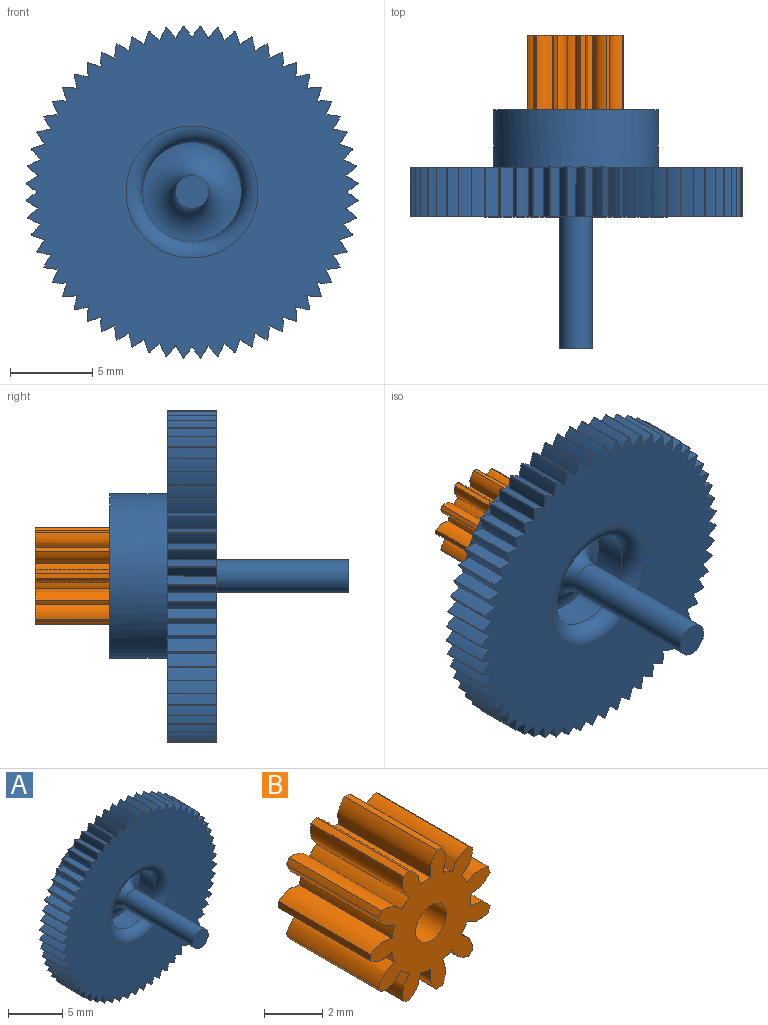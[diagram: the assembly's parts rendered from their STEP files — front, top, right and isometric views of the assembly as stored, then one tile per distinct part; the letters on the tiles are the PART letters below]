
ASSEMBLY  parts=2 mates=1
PART A: 189 faces, bbox 20.1x14.5x20.1 mm
  f0: cylinder r=10.08mm len=3mm, axis (0,1,0), area 0.1mm2, adj f59,f61,f178,f181
  f1: cylinder r=10.08mm len=3mm, axis (0,1,0), area 0.1mm2, adj f59,f61,f176,f179
  f2: cylinder r=10.08mm len=3mm, axis (0,1,0), area 0.1mm2, adj f59,f61,f174,f177
  f3: cylinder r=10.08mm len=3mm, axis (0,1,0), area 0.1mm2, adj f59,f61,f172,f175
  f4: cylinder r=10.08mm len=3mm, axis (0,1,0), area 0.1mm2, adj f59,f61,f170,f173
  f5: cylinder r=10.08mm len=3mm, axis (0,1,0), area 0.1mm2, adj f59,f61,f168,f171
  f6: cylinder r=10.08mm len=3mm, axis (0,1,0), area 0.1mm2, adj f59,f61,f166,f169
  f7: cylinder r=10.08mm len=3mm, axis (0,1,0), area 0.1mm2, adj f59,f61,f160,f167
  f8: cylinder r=10.08mm len=3mm, axis (0,1,0), area 0.1mm2, adj f59,f61,f156,f165
  f9: cylinder r=10.08mm len=3mm, axis (0,1,0), area 0.1mm2, adj f59,f61,f163,f164
  f10: cylinder r=10.08mm len=3mm, axis (0,1,0), area 0.1mm2, adj f59,f61,f158,f161
  f11: cylinder r=10.08mm len=3mm, axis (0,1,0), area 0.1mm2, adj f59,f61,f159,f162
  f12: cylinder r=10.08mm len=3mm, axis (0,1,0), area 0.1mm2, adj f59,f61,f154,f157
  f13: cylinder r=10.08mm len=3mm, axis (0,1,0), area 0.1mm2, adj f59,f61,f152,f155
  f14: cylinder r=10.08mm len=3mm, axis (0,1,0), area 0.1mm2, adj f59,f61,f150,f153
  f15: cylinder r=10.08mm len=3mm, axis (0,1,0), area 0.1mm2, adj f59,f61,f62,f151
  f16: cylinder r=10.08mm len=3mm, axis (0,1,0), area 0.1mm2, adj f59,f61,f149,f180
  f17: cylinder r=10.08mm len=3mm, axis (0,1,0), area 0.1mm2, adj f59,f61,f147,f148
  f18: cylinder r=10.08mm len=3mm, axis (0,1,0), area 0.1mm2, adj f59,f61,f145,f146
  f19: cylinder r=10.08mm len=3mm, axis (0,1,0), area 0.1mm2, adj f59,f61,f143,f144
  f20: cylinder r=10.08mm len=3mm, axis (0,1,0), area 0.1mm2, adj f59,f61,f134,f141
  f21: cylinder r=10.08mm len=3mm, axis (0,1,0), area 0.1mm2, adj f59,f61,f139,f140
  f22: cylinder r=10.08mm len=3mm, axis (0,1,0), area 0.1mm2, adj f59,f61,f137,f142
  f23: cylinder r=10.08mm len=3mm, axis (0,1,0), area 0.1mm2, adj f59,f61,f135,f136
  f24: cylinder r=10.08mm len=3mm, axis (0,1,0), area 0.1mm2, adj f59,f61,f133,f138
  f25: cylinder r=10.08mm len=3mm, axis (0,1,0), area 0.1mm2, adj f59,f61,f131,f132
  f26: cylinder r=10.08mm len=3mm, axis (0,1,0), area 0.1mm2, adj f59,f61,f129,f130
  f27: cylinder r=10.08mm len=3mm, axis (0,1,0), area 0.1mm2, adj f59,f61,f127,f128
  f28: cylinder r=10.08mm len=3mm, axis (0,1,0), area 0.1mm2, adj f59,f61,f125,f126
  f29: cylinder r=10.08mm len=3mm, axis (0,1,0), area 0.1mm2, adj f59,f61,f123,f124
  f30: cylinder r=10.08mm len=3mm, axis (0,1,0), area 0.1mm2, adj f59,f61,f121,f122
  f31: cylinder r=10.08mm len=3mm, axis (0,1,0), area 0.1mm2, adj f59,f61,f119,f120
  f32: cylinder r=10.08mm len=3mm, axis (0,1,0), area 0.1mm2, adj f59,f61,f114,f117
  f33: cylinder r=10.08mm len=3mm, axis (0,1,0), area 0.1mm2, adj f59,f61,f108,f115
  f34: cylinder r=10.08mm len=3mm, axis (0,1,0), area 0.1mm2, adj f59,f61,f113,f116
  f35: cylinder r=10.08mm len=3mm, axis (0,1,0), area 0.1mm2, adj f59,f61,f111,f112
  f36: cylinder r=10.08mm len=3mm, axis (0,1,0), area 0.1mm2, adj f59,f61,f106,f109
  f37: cylinder r=10.08mm len=3mm, axis (0,1,0), area 0.1mm2, adj f59,f61,f104,f107
  f38: cylinder r=10.08mm len=3mm, axis (0,1,0), area 0.1mm2, adj f59,f61,f102,f105
  f39: cylinder r=10.08mm len=3mm, axis (0,1,0), area 0.1mm2, adj f59,f61,f103,f118
  f40: cylinder r=10.08mm len=3mm, axis (0,1,0), area 0.1mm2, adj f59,f61,f101,f110
  f41: cylinder r=10.08mm len=3mm, axis (0,1,0), area 0.1mm2, adj f59,f61,f99,f100
  f42: cylinder r=10.08mm len=3mm, axis (0,1,0), area 0.1mm2, adj f59,f61,f97,f98
  f43: cylinder r=10.08mm len=3mm, axis (0,1,0), area 0.1mm2, adj f59,f61,f95,f96
  f44: cylinder r=10.08mm len=3mm, axis (0,1,0), area 0.1mm2, adj f59,f61,f93,f94
  f45: cylinder r=10.08mm len=3mm, axis (0,1,0), area 0.1mm2, adj f59,f61,f91,f92
  f46: cylinder r=10.08mm len=3mm, axis (0,1,0), area 0.1mm2, adj f59,f61,f89,f90
  f47: cylinder r=10.08mm len=3mm, axis (0,1,0), area 0.1mm2, adj f59,f61,f87,f88
  f48: cylinder r=10.08mm len=3mm, axis (0,1,0), area 0.1mm2, adj f59,f61,f82,f85
  f49: cylinder r=10.08mm len=3mm, axis (0,1,0), area 0.1mm2, adj f59,f61,f78,f83
  f50: cylinder r=10.08mm len=3mm, axis (0,1,0), area 0.1mm2, adj f59,f61,f74,f81
  f51: cylinder r=10.08mm len=3mm, axis (0,1,0), area 0.1mm2, adj f59,f61,f79,f80
  f52: cylinder r=10.08mm len=3mm, axis (0,1,0), area 0.1mm2, adj f59,f61,f72,f77
  f53: cylinder r=10.08mm len=3mm, axis (0,1,0), area 0.1mm2, adj f59,f61,f75,f76
  f54: cylinder r=10.08mm len=3mm, axis (0,1,0), area 0.1mm2, adj f59,f61,f70,f73
  f55: cylinder r=10.08mm len=3mm, axis (0,1,0), area 0.1mm2, adj f59,f61,f71,f86
  f56: cylinder r=10.08mm len=3mm, axis (0,1,0), area 0.1mm2, adj f59,f61,f69,f84
  f57: cylinder r=10.08mm len=3mm, axis (0,1,0), area 0.1mm2, adj f59,f61,f67,f68
  f58: cylinder r=10.08mm len=3mm, axis (0,1,0), area 0.1mm2, adj f59,f61,f65,f66
  f59: plane 20.12x20.12mm, normal (0,-1,0), area 248.2mm2, adj f0,f1,f2,f3,f4,f5,f6,f7
  f60: cylinder r=10.08mm len=3mm, axis (0,1,0), area 0.1mm2, adj f59,f61,f63,f64
  f61: plane 20.12x20.12mm, normal (0,1,0), area 219.9mm2, adj f0,f1,f2,f3,f4,f5,f6,f7
  f62: extruded ~3x0.69mm, area 2.6mm2, adj f15,f59,f61,f63
  f63: extruded ~3x0.69mm, area 2.6mm2, adj f59,f60,f61,f62
  f64: extruded ~3x0.74mm, area 2.6mm2, adj f59,f60,f61,f65
  f65: extruded ~3x0.64mm, area 2.6mm2, adj f58,f59,f61,f64
  f66: extruded ~3x0.78mm, area 2.6mm2, adj f58,f59,f61,f67
  f67: extruded ~3x0.64mm, area 2.6mm2, adj f57,f59,f61,f66
  f68: extruded ~3x0.82mm, area 2.6mm2, adj f57,f59,f61,f69
  f69: extruded ~3x0.7mm, area 2.6mm2, adj f56,f59,f61,f68
  f70: extruded ~3x0.74mm, area 2.6mm2, adj f54,f59,f61,f71
  f71: extruded ~3x0.84mm, area 2.6mm2, adj f55,f59,f61,f70
  f72: extruded ~3x0.79mm, area 2.6mm2, adj f52,f59,f61,f73
  f73: extruded ~3x0.85mm, area 2.6mm2, adj f54,f59,f61,f72
  f74: extruded ~3x0.84mm, area 2.6mm2, adj f50,f59,f61,f75
  f75: extruded ~3x0.85mm, area 2.6mm2, adj f53,f59,f61,f74
  f76: extruded ~3x0.82mm, area 2.6mm2, adj f53,f59,f61,f77
  f77: extruded ~3x0.86mm, area 2.6mm2, adj f52,f59,f61,f76
  f78: extruded ~3x0.86mm, area 2.6mm2, adj f49,f59,f61,f79
  f79: extruded ~3x0.82mm, area 2.6mm2, adj f51,f59,f61,f78
  f80: extruded ~3x0.85mm, area 2.6mm2, adj f51,f59,f61,f81
  f81: extruded ~3x0.84mm, area 2.6mm2, adj f50,f59,f61,f80
  f82: extruded ~3x0.85mm, area 2.6mm2, adj f48,f59,f61,f83
  f83: extruded ~3x0.79mm, area 2.6mm2, adj f49,f59,f61,f82
  f84: extruded ~3x0.84mm, area 2.6mm2, adj f56,f59,f61,f85
  f85: extruded ~3x0.74mm, area 2.6mm2, adj f48,f59,f61,f84
  f86: extruded ~3x0.7mm, area 2.6mm2, adj f55,f59,f61,f87
  f87: extruded ~3x0.82mm, area 2.6mm2, adj f47,f59,f61,f86
  f88: extruded ~3x0.64mm, area 2.6mm2, adj f47,f59,f61,f89
  f89: extruded ~3x0.78mm, area 2.6mm2, adj f46,f59,f61,f88
  f90: extruded ~3x0.64mm, area 2.6mm2, adj f46,f59,f61,f91
  f91: extruded ~3x0.74mm, area 2.6mm2, adj f45,f59,f61,f90
  f92: extruded ~3x0.69mm, area 2.6mm2, adj f45,f59,f61,f93
  f93: extruded ~3x0.69mm, area 2.6mm2, adj f44,f59,f61,f92
  f94: extruded ~3x0.74mm, area 2.6mm2, adj f44,f59,f61,f95
  f95: extruded ~3x0.64mm, area 2.6mm2, adj f43,f59,f61,f94
  f96: extruded ~3x0.78mm, area 2.6mm2, adj f43,f59,f61,f97
  f97: extruded ~3x0.64mm, area 2.6mm2, adj f42,f59,f61,f96
  f98: extruded ~3x0.82mm, area 2.6mm2, adj f42,f59,f61,f99
  f99: extruded ~3x0.7mm, area 2.6mm2, adj f41,f59,f61,f98
  f100: extruded ~3x0.84mm, area 2.6mm2, adj f41,f59,f61,f101
  f101: extruded ~3x0.74mm, area 2.6mm2, adj f40,f59,f61,f100
  f102: extruded ~3x0.7mm, area 2.6mm2, adj f38,f59,f61,f103
  f103: extruded ~3x0.82mm, area 2.6mm2, adj f39,f59,f61,f102
  f104: extruded ~3x0.74mm, area 2.6mm2, adj f37,f59,f61,f105
  f105: extruded ~3x0.84mm, area 2.6mm2, adj f38,f59,f61,f104
  f106: extruded ~3x0.79mm, area 2.6mm2, adj f36,f59,f61,f107
  f107: extruded ~3x0.85mm, area 2.6mm2, adj f37,f59,f61,f106
  f108: extruded ~3x0.82mm, area 2.6mm2, adj f33,f59,f61,f109
  f109: extruded ~3x0.86mm, area 2.6mm2, adj f36,f59,f61,f108
  f110: extruded ~3x0.85mm, area 2.6mm2, adj f40,f59,f61,f111
  f111: extruded ~3x0.79mm, area 2.6mm2, adj f35,f59,f61,f110
  f112: extruded ~3x0.86mm, area 2.6mm2, adj f35,f59,f61,f113
  f113: extruded ~3x0.82mm, area 2.6mm2, adj f34,f59,f61,f112
  f114: extruded ~3x0.84mm, area 2.6mm2, adj f32,f59,f61,f115
  f115: extruded ~3x0.85mm, area 2.6mm2, adj f33,f59,f61,f114
  f116: extruded ~3x0.85mm, area 2.6mm2, adj f34,f59,f61,f117
  f117: extruded ~3x0.84mm, area 2.6mm2, adj f32,f59,f61,f116
  f118: extruded ~3x0.64mm, area 2.6mm2, adj f39,f59,f61,f119
  f119: extruded ~3x0.78mm, area 2.6mm2, adj f31,f59,f61,f118
  f120: extruded ~3x0.64mm, area 2.6mm2, adj f31,f59,f61,f121
  f121: extruded ~3x0.74mm, area 2.6mm2, adj f30,f59,f61,f120
  f122: extruded ~3x0.69mm, area 2.6mm2, adj f30,f59,f61,f123
  f123: extruded ~3x0.69mm, area 2.6mm2, adj f29,f59,f61,f122
  f124: extruded ~3x0.74mm, area 2.6mm2, adj f29,f59,f61,f125
  f125: extruded ~3x0.64mm, area 2.6mm2, adj f28,f59,f61,f124
  f126: extruded ~3x0.78mm, area 2.6mm2, adj f28,f59,f61,f127
  f127: extruded ~3x0.64mm, area 2.6mm2, adj f27,f59,f61,f126
  f128: extruded ~3x0.82mm, area 2.6mm2, adj f27,f59,f61,f129
  f129: extruded ~3x0.7mm, area 2.6mm2, adj f26,f59,f61,f128
  f130: extruded ~3x0.84mm, area 2.6mm2, adj f26,f59,f61,f131
  f131: extruded ~3x0.74mm, area 2.6mm2, adj f25,f59,f61,f130
  f132: extruded ~3x0.85mm, area 2.6mm2, adj f25,f59,f61,f133
  f133: extruded ~3x0.79mm, area 2.6mm2, adj f24,f59,f61,f132
  f134: extruded ~3x0.84mm, area 2.6mm2, adj f20,f59,f61,f135
  f135: extruded ~3x0.85mm, area 2.6mm2, adj f23,f59,f61,f134
  f136: extruded ~3x0.82mm, area 2.6mm2, adj f23,f59,f61,f137
  f137: extruded ~3x0.86mm, area 2.6mm2, adj f22,f59,f61,f136
  f138: extruded ~3x0.86mm, area 2.6mm2, adj f24,f59,f61,f139
  f139: extruded ~3x0.82mm, area 2.6mm2, adj f21,f59,f61,f138
  f140: extruded ~3x0.85mm, area 2.6mm2, adj f21,f59,f61,f141
  f141: extruded ~3x0.84mm, area 2.6mm2, adj f20,f59,f61,f140
  f142: extruded ~3x0.79mm, area 2.6mm2, adj f22,f59,f61,f143
  f143: extruded ~3x0.85mm, area 2.6mm2, adj f19,f59,f61,f142
  f144: extruded ~3x0.74mm, area 2.6mm2, adj f19,f59,f61,f145
  f145: extruded ~3x0.84mm, area 2.6mm2, adj f18,f59,f61,f144
  f146: extruded ~3x0.7mm, area 2.6mm2, adj f18,f59,f61,f147
  f147: extruded ~3x0.82mm, area 2.6mm2, adj f17,f59,f61,f146
  f148: extruded ~3x0.64mm, area 2.6mm2, adj f17,f59,f61,f149
  f149: extruded ~3x0.78mm, area 2.6mm2, adj f16,f59,f61,f148
  f150: extruded ~3x0.64mm, area 2.6mm2, adj f14,f59,f61,f151
  f151: extruded ~3x0.74mm, area 2.6mm2, adj f15,f59,f61,f150
  f152: extruded ~3x0.64mm, area 2.6mm2, adj f13,f59,f61,f153
  f153: extruded ~3x0.78mm, area 2.6mm2, adj f14,f59,f61,f152
  f154: extruded ~3x0.7mm, area 2.6mm2, adj f12,f59,f61,f155
  f155: extruded ~3x0.82mm, area 2.6mm2, adj f13,f59,f61,f154
  f156: extruded ~3x0.74mm, area 2.6mm2, adj f8,f59,f61,f157
  f157: extruded ~3x0.84mm, area 2.6mm2, adj f12,f59,f61,f156
  f158: extruded ~3x0.84mm, area 2.6mm2, adj f10,f59,f61,f159
  f159: extruded ~3x0.85mm, area 2.6mm2, adj f11,f59,f61,f158
  f160: extruded ~3x0.85mm, area 2.6mm2, adj f7,f59,f61,f161
  f161: extruded ~3x0.84mm, area 2.6mm2, adj f10,f59,f61,f160
  f162: extruded ~3x0.82mm, area 2.6mm2, adj f11,f59,f61,f163
  f163: extruded ~3x0.86mm, area 2.6mm2, adj f9,f59,f61,f162
  f164: extruded ~3x0.79mm, area 2.6mm2, adj f9,f59,f61,f165
  f165: extruded ~3x0.85mm, area 2.6mm2, adj f8,f59,f61,f164
  f166: extruded ~3x0.86mm, area 2.6mm2, adj f6,f59,f61,f167
  f167: extruded ~3x0.82mm, area 2.6mm2, adj f7,f59,f61,f166
  f168: extruded ~3x0.85mm, area 2.6mm2, adj f5,f59,f61,f169
  f169: extruded ~3x0.79mm, area 2.6mm2, adj f6,f59,f61,f168
  f170: extruded ~3x0.84mm, area 2.6mm2, adj f4,f59,f61,f171
  f171: extruded ~3x0.74mm, area 2.6mm2, adj f5,f59,f61,f170
  f172: extruded ~3x0.82mm, area 2.6mm2, adj f3,f59,f61,f173
  f173: extruded ~3x0.7mm, area 2.6mm2, adj f4,f59,f61,f172
  f174: extruded ~3x0.78mm, area 2.6mm2, adj f2,f59,f61,f175
  f175: extruded ~3x0.64mm, area 2.6mm2, adj f3,f59,f61,f174
  f176: extruded ~3x0.74mm, area 2.6mm2, adj f1,f59,f61,f177
  f177: extruded ~3x0.64mm, area 2.6mm2, adj f2,f59,f61,f176
  f178: extruded ~3x0.69mm, area 2.6mm2, adj f0,f59,f61,f179
  f179: extruded ~3x0.69mm, area 2.6mm2, adj f1,f59,f61,f178
  f180: extruded ~3x0.64mm, area 2.6mm2, adj f16,f59,f61,f181
  f181: extruded ~3x0.74mm, area 2.6mm2, adj f0,f59,f61,f180
  f182: cylinder r=5mm len=10mm, axis (0,-1,0), area 110mm2, adj f61,f183
  f183: plane 10x10mm, normal (0,1,0), area 78.5mm2, adj f182
  f184: cylinder r=3mm len=6mm, axis (0,-1,0), area 37.7mm2, adj f187,f188
  f185: cylinder r=1mm len=9mm, axis (0,1,0), area 56.5mm2, adj f186,f188
  f186: plane 2x2mm, normal (0,-1,0), area 3.1mm2, adj f185
  f187: torus R=4mm, axis (0,-1,0), area 33.2mm2, adj f59,f184
  f188: torus R=3mm, axis (0,-1,0), area 34.1mm2, adj f184,f185
PART B: 47 faces, bbox 5.9x4.5x5.9 mm
  f0: cylinder r=2.95mm len=4.5mm, axis (0,1,0), area 1.2mm2, adj f12,f13,f29,f46
  f1: cylinder r=2.95mm len=4.5mm, axis (0,1,0), area 1.2mm2, adj f12,f13,f43,f44
  f2: cylinder r=2.95mm len=4.5mm, axis (0,1,0), area 1.2mm2, adj f12,f13,f35,f40
  f3: cylinder r=2.95mm len=4.5mm, axis (0,1,0), area 1.2mm2, adj f12,f13,f37,f41
  f4: cylinder r=2.95mm len=4.5mm, axis (0,1,0), area 1.2mm2, adj f12,f13,f23,f34
  f5: cylinder r=2.95mm len=4.5mm, axis (0,1,0), area 1.2mm2, adj f12,f13,f31,f32
  f6: cylinder r=2.95mm len=4.5mm, axis (0,1,0), area 1.2mm2, adj f12,f13,f14,f28
  f7: cylinder r=2.95mm len=4.5mm, axis (0,1,0), area 1.2mm2, adj f12,f13,f25,f26
  f8: cylinder r=2.95mm len=4.5mm, axis (0,1,0), area 1.2mm2, adj f12,f13,f17,f22
  f9: cylinder r=2.95mm len=4.5mm, axis (0,1,0), area 1.2mm2, adj f12,f13,f19,f38
  f10: cylinder r=0.75mm len=4.5mm, axis (0,1,0), area 21.2mm2, adj f12,f13
  f11: cylinder r=2.95mm len=4.5mm, axis (0,1,0), area 1.2mm2, adj f12,f13,f16,f20
  f12: plane 5.92x5.86mm, normal (0,-1,0), area 16.9mm2, adj f0,f1,f2,f3,f4,f5,f6,f7
  f13: plane 5.92x5.86mm, normal (0,1,0), area 16.9mm2, adj f0,f1,f2,f3,f4,f5,f6,f7
  f14: extruded ~4.5x0.95mm, area 5mm2, adj f6,f12,f13,f15
  f15: cylinder r=1.93mm len=4.5mm, axis (0,1,0), area 2.2mm2, adj f12,f13,f14,f16
  f16: extruded ~4.5x0.95mm, area 5mm2, adj f11,f12,f13,f15
  f17: extruded ~4.5x0.81mm, area 5mm2, adj f8,f12,f13,f18
  f18: cylinder r=1.93mm len=4.5mm, axis (0,1,0), area 2.2mm2, adj f12,f13,f17,f19
  f19: extruded ~4.5x1.06mm, area 5mm2, adj f9,f12,f13,f18
  f20: extruded ~4.5x1.05mm, area 5mm2, adj f11,f12,f13,f21
  f21: cylinder r=1.93mm len=4.5mm, axis (0,1,0), area 2.2mm2, adj f12,f13,f20,f22
  f22: extruded ~4.5x0.9mm, area 5mm2, adj f8,f12,f13,f21
  f23: extruded ~4.5x1.06mm, area 5mm2, adj f4,f12,f13,f24
  f24: cylinder r=1.93mm len=4.5mm, axis (0,1,0), area 2.2mm2, adj f12,f13,f23,f25
  f25: extruded ~4.5x0.81mm, area 5mm2, adj f7,f12,f13,f24
  f26: extruded ~4.5x0.9mm, area 5mm2, adj f7,f12,f13,f27
  f27: cylinder r=1.93mm len=4.5mm, axis (0,1,0), area 2.2mm2, adj f12,f13,f26,f28
  f28: extruded ~4.5x1.05mm, area 5mm2, adj f6,f12,f13,f27
  f29: extruded ~4.5x0.97mm, area 5mm2, adj f0,f12,f13,f30
  f30: cylinder r=1.93mm len=4.5mm, axis (0,1,0), area 2.2mm2, adj f12,f13,f29,f31
  f31: extruded ~4.5x1.02mm, area 5mm2, adj f5,f12,f13,f30
  f32: extruded ~4.5x0.88mm, area 5mm2, adj f5,f12,f13,f33
  f33: cylinder r=1.93mm len=4.5mm, axis (0,1,0), area 2.2mm2, adj f12,f13,f32,f34
  f34: extruded ~4.5x1.01mm, area 5mm2, adj f4,f12,f13,f33
  f35: extruded ~4.5x1.02mm, area 5mm2, adj f2,f12,f13,f36
  f36: cylinder r=1.93mm len=4.5mm, axis (0,1,0), area 2.2mm2, adj f12,f13,f35,f37
  f37: extruded ~4.5x0.97mm, area 5mm2, adj f3,f12,f13,f36
  f38: extruded ~4.5x1.01mm, area 5mm2, adj f9,f12,f13,f39
  f39: cylinder r=1.93mm len=4.5mm, axis (0,1,0), area 2.2mm2, adj f12,f13,f38,f40
  f40: extruded ~4.5x0.88mm, area 5mm2, adj f2,f12,f13,f39
  f41: extruded ~4.5x0.79mm, area 5mm2, adj f3,f12,f13,f42
  f42: cylinder r=1.93mm len=4.5mm, axis (0,1,0), area 2.2mm2, adj f12,f13,f41,f43
  f43: extruded ~4.5x1.04mm, area 5mm2, adj f1,f12,f13,f42
  f44: extruded ~4.5x1.04mm, area 5mm2, adj f1,f12,f13,f45
  f45: cylinder r=1.93mm len=4.5mm, axis (0,1,0), area 2.2mm2, adj f12,f13,f44,f46
  f46: extruded ~4.5x0.79mm, area 5mm2, adj f0,f12,f13,f45
PLACE A t=(-14.95,-7.82,-1.4)mm
PLACE B t=(-14.95,0.18,-1.4)mm
MATE parallel B.f0 <-> A.f182  axis (0,-1,0) through (-14.95,-4.32,-1.4)mm
